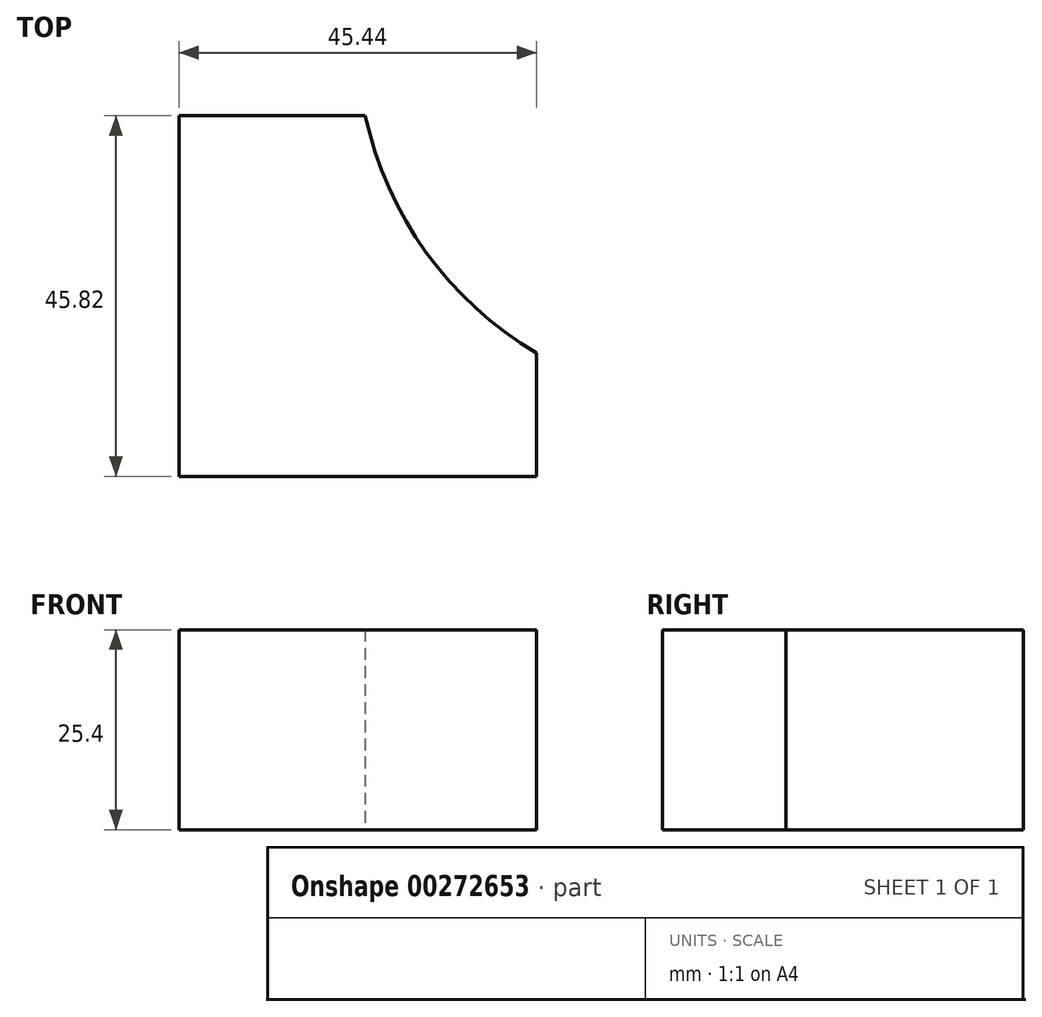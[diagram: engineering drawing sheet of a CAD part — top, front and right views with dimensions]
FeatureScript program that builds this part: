
annotation { "Feature Type Name" : "Feature", "Feature Type Description" : "" }
export const myFeature = defineFeature(function(context is Context, id is Id, definition is map)
    precondition{}
    {
        {
            var Q0;
            Q0=qCreatedBy(makeId("Top.planeOp"),FACE);
            var sketch = newSketch(context, id + "F0", { "sketchPlane" : qUnion([Q0])});
            skLineSegment(sketch, "E0", {"start": v(-66.64, 68.93) * mm, "end": v(-42.96, 68.93) * mm});
            skLineSegment(sketch, "E1", {"start": v(-66.64, 68.93) * mm, "end": v(-66.64, 23.1) * mm});
            skLineSegment(sketch, "E2", {"start": v(-66.64, 23.1) * mm, "end": v(-21.2, 23.1) * mm});
            skLineSegment(sketch, "E3", {"start": v(-21.2, 23.1) * mm, "end": v(-21.2, 38.76) * mm});
            skArc(sketch, "E4", {"start": v(-42.96, 68.93) * mm, "mid": v(-35.24, 51.57) * mm, "end": v(-21.2, 38.76) * mm});
            skSolve(sketch);
        }
        {
            var Q0;
            Q0 = qSketchRegion(id + "F0", true);
            extrude(context, id + "F1", {"entities" : qUnion([Q0]), "depth" : 25.4 * mm});
        }
    });
